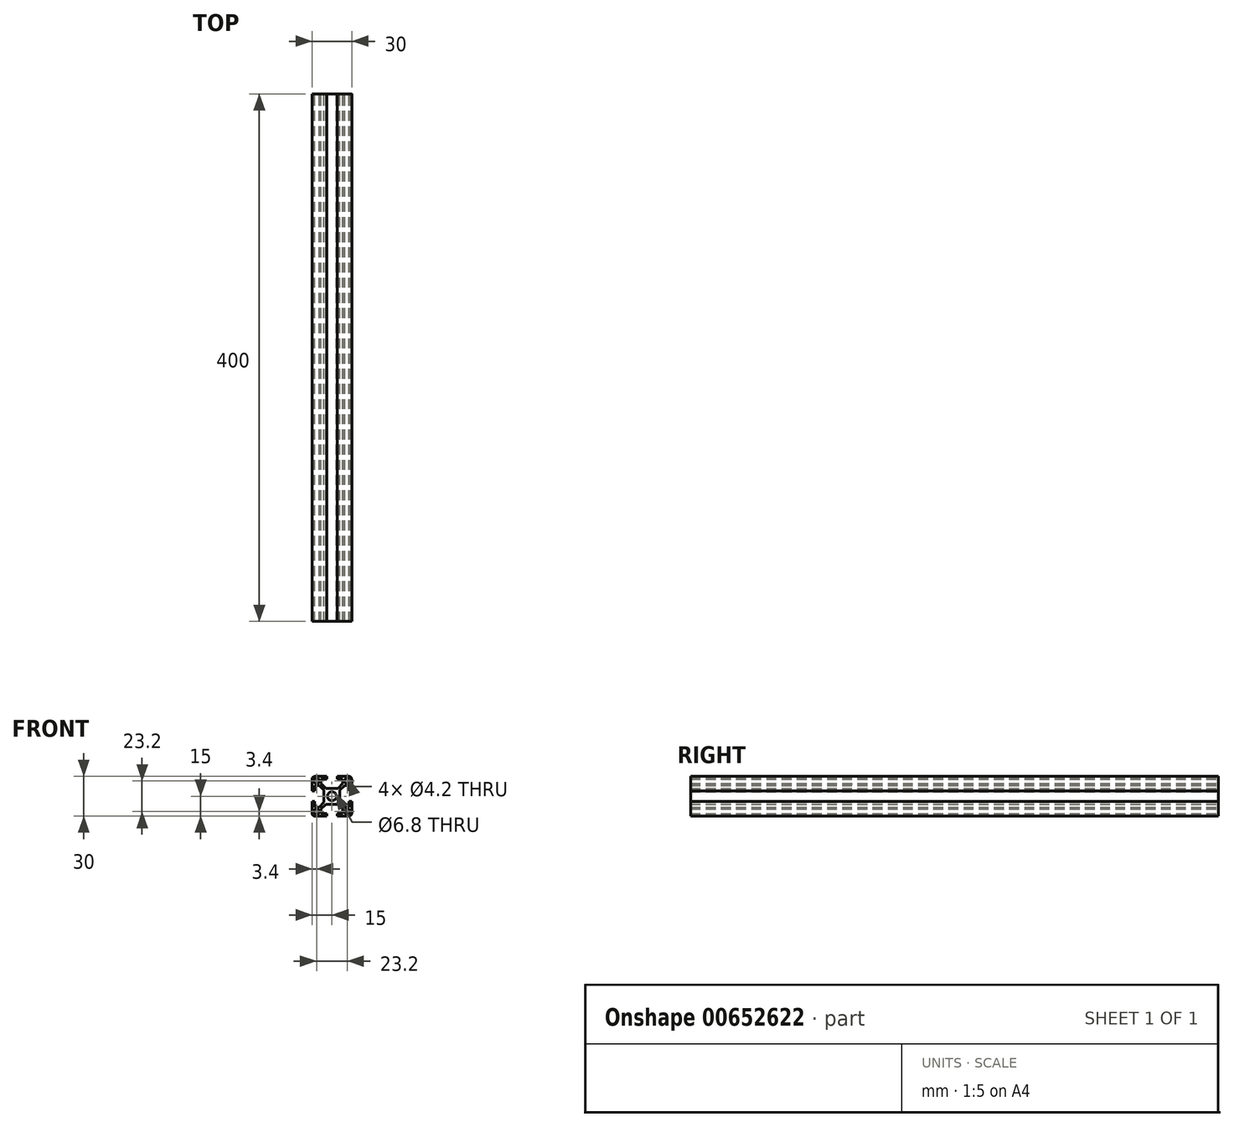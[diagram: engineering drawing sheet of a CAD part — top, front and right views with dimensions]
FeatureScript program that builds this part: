
annotation { "Feature Type Name" : "Feature", "Feature Type Description" : "" }
export const myFeature = defineFeature(function(context is Context, id is Id, definition is map)
    precondition{}
    {
        {
            var Q0;
            Q0=qCreatedBy(makeId("Front.planeOp"),FACE);
            var sketch = newSketch(context, id + "F0", { "sketchPlane" : qUnion([Q0])});
            skLineSegment(sketch, "E0", {"start": v(0, 6) * mm, "end": v(-4.59, 6) * mm});
            skLineSegment(sketch, "E1", {"start": v(-4.59, 6) * mm, "end": v(-8.25, 9.66) * mm});
            skLineSegment(sketch, "E2", {"start": v(-8.25, 9.66) * mm, "end": v(-8.25, 13) * mm});
            skLineSegment(sketch, "E3", {"start": v(-8.25, 13) * mm, "end": v(-4, 13) * mm});
            skLineSegment(sketch, "E4", {"start": v(-4, 13) * mm, "end": v(-4, 15) * mm});
            skLineSegment(sketch, "E5", {"start": v(-4, 15) * mm, "end": v(-13, 15) * mm});
            skLineSegment(sketch, "E6", {"start": v(-15, 13) * mm, "end": v(-15, 4) * mm});
            skLineSegment(sketch, "E7", {"start": v(-15, 4) * mm, "end": v(-13, 4) * mm});
            skLineSegment(sketch, "E8", {"start": v(-13, 4) * mm, "end": v(-13, 8.25) * mm});
            skLineSegment(sketch, "E9", {"start": v(-13, 8.25) * mm, "end": v(-9.66, 8.25) * mm});
            skLineSegment(sketch, "E10", {"start": v(-9.66, 8.25) * mm, "end": v(-6, 4.59) * mm});
            skLineSegment(sketch, "E11", {"start": v(-6, 4.59) * mm, "end": v(-6, 0) * mm});
            skLineSegment(sketch, "E12", {"start": v(-6, 0) * mm, "end": v(0, 0) * mm, "construction": true});
            skLineSegment(sketch, "E13", {"start": v(0, 0) * mm, "end": v(0, 6) * mm, "construction": true});
            skArc(sketch, "E14", {"start": v(0, 3.4) * mm, "mid": v(-2.4, 2.4) * mm, "end": v(-3.4, 0) * mm});
            skCircle(sketch, "E15", {"center": v(-11.6, 11.6) * mm, "radius": 2.1 * mm});
            skLineSegment(sketch, "E16", {"start": v(0, 0) * mm, "end": v(-7.38, 7.38) * mm, "construction": true});
            skLineSegment(sketch, "E17.1.0", {"start": v(-8.25, -13) * mm, "end": v(-8.25, -9.66) * mm});
            skLineSegment(sketch, "E17.1.1", {"start": v(-4, -15) * mm, "end": v(-4, -13) * mm});
            skLineSegment(sketch, "E17.1.2", {"start": v(-4, -13) * mm, "end": v(-8.25, -13) * mm});
            skLineSegment(sketch, "E17.1.3", {"start": v(-15, -4) * mm, "end": v(-15, -13) * mm});
            skLineSegment(sketch, "E17.1.4", {"start": v(-8.25, -9.66) * mm, "end": v(-4.59, -6) * mm});
            skLineSegment(sketch, "E17.1.5", {"start": v(-13, -15) * mm, "end": v(-4, -15) * mm});
            skLineSegment(sketch, "E17.1.6", {"start": v(-4.59, -6) * mm, "end": v(0, -6) * mm});
            skLineSegment(sketch, "E17.1.7", {"start": v(0, -6) * mm, "end": v(0, 0) * mm, "construction": true});
            skLineSegment(sketch, "E17.1.8", {"start": v(0, 0) * mm, "end": v(-6, 0) * mm, "construction": true});
            skLineSegment(sketch, "E17.1.9", {"start": v(-13, -4) * mm, "end": v(-15, -4) * mm});
            skLineSegment(sketch, "E17.1.10", {"start": v(-13, -8.25) * mm, "end": v(-13, -4) * mm});
            skArc(sketch, "E17.1.11", {"start": v(-3.4, 0) * mm, "mid": v(-2.4, -2.4) * mm, "end": v(0, -3.4) * mm});
            skLineSegment(sketch, "E17.1.12", {"start": v(-9.66, -8.25) * mm, "end": v(-13, -8.25) * mm});
            skLineSegment(sketch, "E17.1.13", {"start": v(0, 0) * mm, "end": v(-7.38, -7.38) * mm, "construction": true});
            skLineSegment(sketch, "E17.1.14", {"start": v(-6, -4.59) * mm, "end": v(-9.66, -8.25) * mm});
            skCircle(sketch, "E17.1.15", {"center": v(-11.6, -11.6) * mm, "radius": 2.1 * mm});
            skLineSegment(sketch, "E17.1.16", {"start": v(-6, 0) * mm, "end": v(-6, -4.59) * mm});
            skLineSegment(sketch, "E17.2.0", {"start": v(13, -8.25) * mm, "end": v(9.66, -8.25) * mm});
            skLineSegment(sketch, "E17.2.1", {"start": v(15, -4) * mm, "end": v(13, -4) * mm});
            skLineSegment(sketch, "E17.2.2", {"start": v(13, -4) * mm, "end": v(13, -8.25) * mm});
            skLineSegment(sketch, "E17.2.3", {"start": v(4, -15) * mm, "end": v(13, -15) * mm});
            skLineSegment(sketch, "E17.2.4", {"start": v(9.66, -8.25) * mm, "end": v(6, -4.59) * mm});
            skLineSegment(sketch, "E17.2.5", {"start": v(15, -13) * mm, "end": v(15, -4) * mm});
            skLineSegment(sketch, "E17.2.6", {"start": v(6, -4.59) * mm, "end": v(6, 0) * mm});
            skLineSegment(sketch, "E17.2.7", {"start": v(6, 0) * mm, "end": v(0, 0) * mm, "construction": true});
            skLineSegment(sketch, "E17.2.8", {"start": v(0, 0) * mm, "end": v(0, -6) * mm, "construction": true});
            skLineSegment(sketch, "E17.2.9", {"start": v(4, -13) * mm, "end": v(4, -15) * mm});
            skLineSegment(sketch, "E17.2.10", {"start": v(8.25, -13) * mm, "end": v(4, -13) * mm});
            skArc(sketch, "E17.2.11", {"start": v(0, -3.4) * mm, "mid": v(2.4, -2.4) * mm, "end": v(3.4, 0) * mm});
            skLineSegment(sketch, "E17.2.12", {"start": v(8.25, -9.66) * mm, "end": v(8.25, -13) * mm});
            skLineSegment(sketch, "E17.2.13", {"start": v(0, 0) * mm, "end": v(7.38, -7.38) * mm, "construction": true});
            skLineSegment(sketch, "E17.2.14", {"start": v(4.59, -6) * mm, "end": v(8.25, -9.66) * mm});
            skCircle(sketch, "E17.2.15", {"center": v(11.6, -11.6) * mm, "radius": 2.1 * mm});
            skLineSegment(sketch, "E17.2.16", {"start": v(0, -6) * mm, "end": v(4.59, -6) * mm});
            skLineSegment(sketch, "E17.3.0", {"start": v(8.25, 13) * mm, "end": v(8.25, 9.66) * mm});
            skLineSegment(sketch, "E17.3.1", {"start": v(4, 15) * mm, "end": v(4, 13) * mm});
            skLineSegment(sketch, "E17.3.2", {"start": v(4, 13) * mm, "end": v(8.25, 13) * mm});
            skLineSegment(sketch, "E17.3.3", {"start": v(15, 4) * mm, "end": v(15, 13) * mm});
            skLineSegment(sketch, "E17.3.4", {"start": v(8.25, 9.66) * mm, "end": v(4.59, 6) * mm});
            skLineSegment(sketch, "E17.3.5", {"start": v(13, 15) * mm, "end": v(4, 15) * mm});
            skLineSegment(sketch, "E17.3.6", {"start": v(4.59, 6) * mm, "end": v(0, 6) * mm});
            skLineSegment(sketch, "E17.3.7", {"start": v(0, 6) * mm, "end": v(0, 0) * mm, "construction": true});
            skLineSegment(sketch, "E17.3.8", {"start": v(0, 0) * mm, "end": v(6, 0) * mm, "construction": true});
            skLineSegment(sketch, "E17.3.9", {"start": v(13, 4) * mm, "end": v(15, 4) * mm});
            skLineSegment(sketch, "E17.3.10", {"start": v(13, 8.25) * mm, "end": v(13, 4) * mm});
            skArc(sketch, "E17.3.11", {"start": v(3.4, 0) * mm, "mid": v(2.4, 2.4) * mm, "end": v(0, 3.4) * mm});
            skLineSegment(sketch, "E17.3.12", {"start": v(9.66, 8.25) * mm, "end": v(13, 8.25) * mm});
            skLineSegment(sketch, "E17.3.13", {"start": v(0, 0) * mm, "end": v(7.38, 7.38) * mm, "construction": true});
            skLineSegment(sketch, "E17.3.14", {"start": v(6, 4.59) * mm, "end": v(9.66, 8.25) * mm});
            skCircle(sketch, "E17.3.15", {"center": v(11.6, 11.6) * mm, "radius": 2.1 * mm});
            skLineSegment(sketch, "E17.3.16", {"start": v(6, 0) * mm, "end": v(6, 4.59) * mm});
            skPoint(sketch, "E18.visualSharp", {"position": v(-15, 15) * mm});
            skArc(sketch, "E18.filletArc", {"start": v(-13, 15) * mm, "mid": v(-14.41, 14.41) * mm, "end": v(-15, 13) * mm});
            skPoint(sketch, "E19.visualSharp", {"position": v(15, 15) * mm});
            skArc(sketch, "E19.filletArc", {"start": v(15, 13) * mm, "mid": v(14.41, 14.41) * mm, "end": v(13, 15) * mm});
            skPoint(sketch, "E20.visualSharp", {"position": v(15, -15) * mm});
            skArc(sketch, "E20.filletArc", {"start": v(13, -15) * mm, "mid": v(14.41, -14.41) * mm, "end": v(15, -13) * mm});
            skPoint(sketch, "E21.visualSharp", {"position": v(-15, -15) * mm});
            skArc(sketch, "E21.filletArc", {"start": v(-15, -13) * mm, "mid": v(-14.41, -14.41) * mm, "end": v(-13, -15) * mm});
            skSolve(sketch);
        }
        {
            var Q0;
            Q0 = qSketchRegion(id + "F0", true);
            extrude(context, id + "F1", {"entities" : qUnion([Q0]), "depth" : 400 * mm, "offsetDistance" : 25 * mm});
        }
    });
